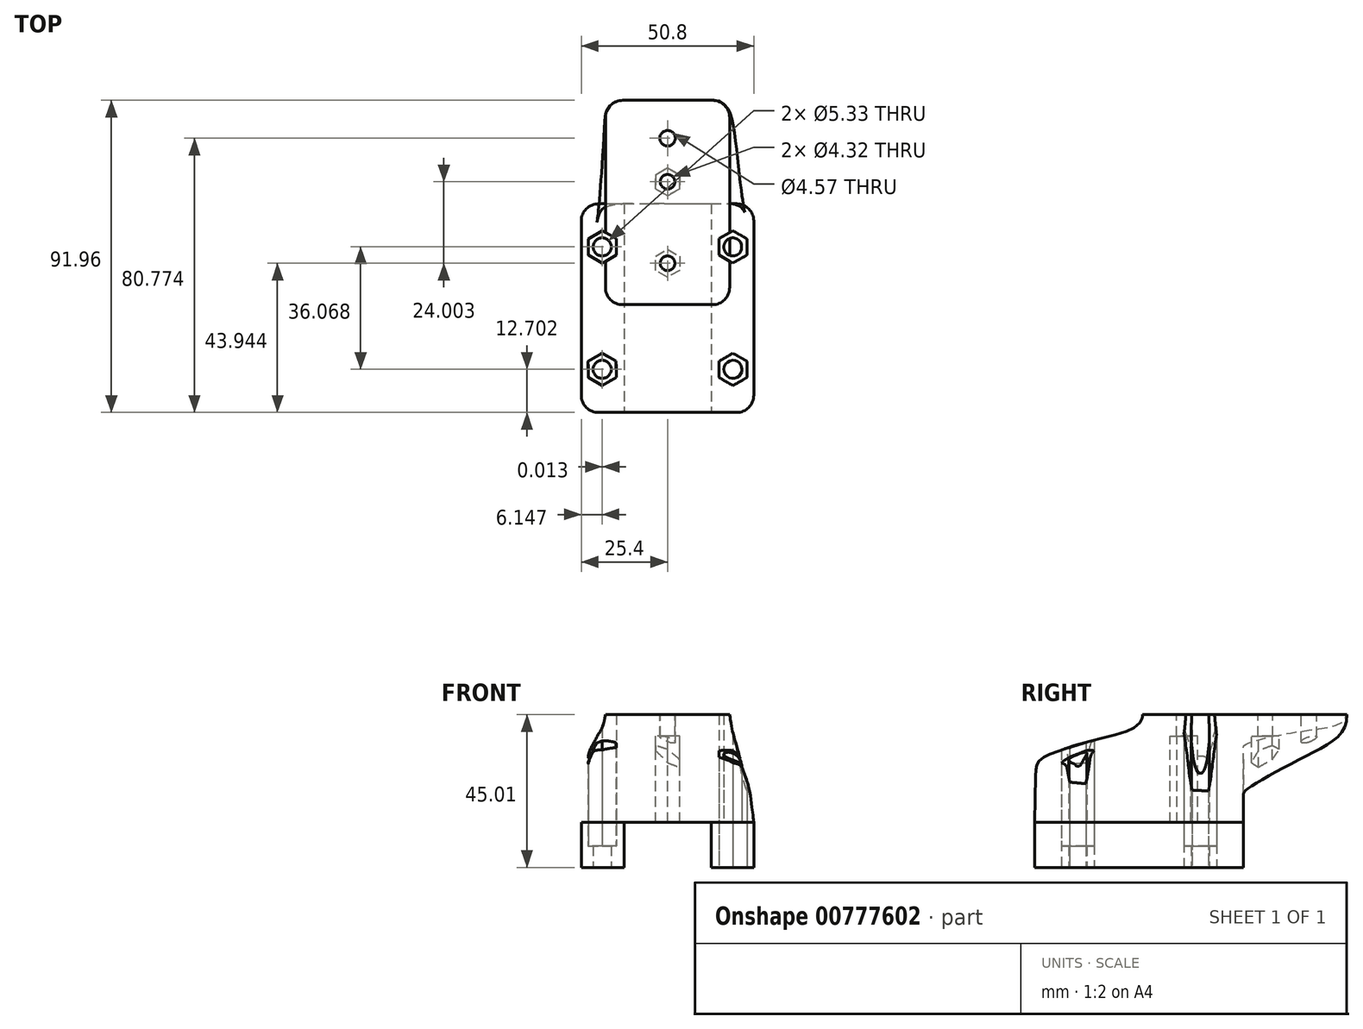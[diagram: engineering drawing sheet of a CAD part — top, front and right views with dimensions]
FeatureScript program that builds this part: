
annotation { "Feature Type Name" : "Feature", "Feature Type Description" : "" }
export const myFeature = defineFeature(function(context is Context, id is Id, definition is map)
    precondition{}
    {
        {
            var Q0;
            Q0=qCreatedBy(makeId("Top.planeOp"),FACE);
            var sketch = newSketch(context, id + "F0", { "sketchPlane" : qUnion([Q0])});
            skLineSegment(sketch, "E0.bottom", {"start": v(-20.32, 0) * mm, "end": v(20.32, 0) * mm});
            skLineSegment(sketch, "E0.top", {"start": v(-20.32, -61.47) * mm, "end": v(20.32, -61.47) * mm});
            skLineSegment(sketch, "E0.left", {"start": v(-25.4, -5.08) * mm, "end": v(-25.4, -56.39) * mm});
            skLineSegment(sketch, "E0.right", {"start": v(25.4, -5.08) * mm, "end": v(25.4, -56.39) * mm});
            skPoint(sketch, "E1.visualSharp", {"position": v(-25.4, 0) * mm});
            skArc(sketch, "E1.filletArc", {"start": v(-20.32, 0) * mm, "mid": v(-23.91, -1.49) * mm, "end": v(-25.4, -5.08) * mm});
            skPoint(sketch, "E2.visualSharp", {"position": v(25.4, 0) * mm});
            skArc(sketch, "E2.filletArc", {"start": v(25.4, -5.08) * mm, "mid": v(23.91, -1.49) * mm, "end": v(20.32, 0) * mm});
            skPoint(sketch, "E3.visualSharp", {"position": v(-25.4, -61.47) * mm});
            skArc(sketch, "E3.filletArc", {"start": v(-25.4, -56.39) * mm, "mid": v(-23.91, -59.98) * mm, "end": v(-20.32, -61.47) * mm});
            skPoint(sketch, "E4.visualSharp", {"position": v(25.4, -61.47) * mm});
            skArc(sketch, "E4.filletArc", {"start": v(20.32, -61.47) * mm, "mid": v(23.91, -59.98) * mm, "end": v(25.4, -56.39) * mm});
            skCircle(sketch, "E5", {"center": v(-19.24, -12.7) * mm, "radius": 2.67 * mm});
            skLineSegment(sketch, "E6.bottom", {"start": v(-12.83, 0) * mm, "end": v(12.83, 0) * mm});
            skLineSegment(sketch, "E6.top", {"start": v(-12.83, -61.47) * mm, "end": v(12.83, -61.47) * mm});
            skLineSegment(sketch, "E6.left", {"start": v(-12.83, 0) * mm, "end": v(-12.83, -61.47) * mm});
            skLineSegment(sketch, "E6.right", {"start": v(12.83, 0) * mm, "end": v(12.83, -61.47) * mm});
            skCircle(sketch, "E7.cCircle", {"center": v(-19.24, -12.7) * mm, "radius": 4.13 * mm, "construction": true});
            skLineSegment(sketch, "E7.0", {"start": v(-15.1, -15.06) * mm, "end": v(-19.22, -17.47) * mm});
            skLineSegment(sketch, "E7.1", {"start": v(-19.22, -17.47) * mm, "end": v(-23.36, -15.1) * mm});
            skLineSegment(sketch, "E7.2", {"start": v(-23.36, -15.1) * mm, "end": v(-23.38, -10.34) * mm});
            skLineSegment(sketch, "E7.3", {"start": v(-23.38, -10.34) * mm, "end": v(-19.26, -7.93) * mm});
            skLineSegment(sketch, "E7.4", {"start": v(-19.26, -7.93) * mm, "end": v(-15.12, -10.3) * mm});
            skLineSegment(sketch, "E7.5", {"start": v(-15.12, -10.3) * mm, "end": v(-15.1, -15.06) * mm});
            skPoint(sketch, "E7.0.midPoint", {"position": v(-17.16, -16.27) * mm});
            skCircle(sketch, "E8", {"center": v(-19.25, -48.77) * mm, "radius": 2.67 * mm});
            skCircle(sketch, "E9.cCircle", {"center": v(-19.25, -48.77) * mm, "radius": 4.13 * mm, "construction": true});
            skLineSegment(sketch, "E9.0", {"start": v(-15.12, -51.13) * mm, "end": v(-19.23, -53.53) * mm});
            skLineSegment(sketch, "E9.1", {"start": v(-19.23, -53.53) * mm, "end": v(-23.37, -51.17) * mm});
            skLineSegment(sketch, "E9.2", {"start": v(-23.37, -51.17) * mm, "end": v(-23.4, -46.4) * mm});
            skLineSegment(sketch, "E9.3", {"start": v(-23.4, -46.4) * mm, "end": v(-19.27, -44) * mm});
            skLineSegment(sketch, "E9.4", {"start": v(-19.27, -44) * mm, "end": v(-15.14, -46.37) * mm});
            skLineSegment(sketch, "E9.5", {"start": v(-15.14, -46.37) * mm, "end": v(-15.12, -51.13) * mm});
            skPoint(sketch, "E9.0.midPoint", {"position": v(-17.17, -52.33) * mm});
            skLineSegment(sketch, "E10.MirrorCS", {"start": v(23.36, -15.1) * mm, "end": v(23.38, -10.34) * mm});
            skLineSegment(sketch, "E11.MirrorCS", {"start": v(23.4, -46.4) * mm, "end": v(19.27, -44) * mm});
            skLineSegment(sketch, "E12.MirrorCS", {"start": v(23.37, -51.17) * mm, "end": v(23.4, -46.4) * mm});
            skLineSegment(sketch, "E13.MirrorCS", {"start": v(19.27, -44) * mm, "end": v(15.14, -46.37) * mm});
            skLineSegment(sketch, "E14.MirrorCS", {"start": v(23.38, -10.34) * mm, "end": v(19.26, -7.93) * mm});
            skLineSegment(sketch, "E15.MirrorCS", {"start": v(15.1, -15.06) * mm, "end": v(19.22, -17.47) * mm});
            skLineSegment(sketch, "E16.MirrorCS", {"start": v(19.26, -7.93) * mm, "end": v(15.12, -10.3) * mm});
            skLineSegment(sketch, "E17.MirrorCS", {"start": v(19.22, -17.47) * mm, "end": v(23.36, -15.1) * mm});
            skLineSegment(sketch, "E18.MirrorCS", {"start": v(15.14, -46.37) * mm, "end": v(15.12, -51.13) * mm});
            skLineSegment(sketch, "E19.MirrorCS", {"start": v(15.12, -51.13) * mm, "end": v(19.23, -53.53) * mm});
            skLineSegment(sketch, "E20.MirrorCS", {"start": v(19.23, -53.53) * mm, "end": v(23.37, -51.17) * mm});
            skLineSegment(sketch, "E21.MirrorCS", {"start": v(15.12, -10.3) * mm, "end": v(15.1, -15.06) * mm});
            skCircle(sketch, "E22.MirrorC", {"center": v(19.25, -48.77) * mm, "radius": 2.67 * mm});
            skCircle(sketch, "E23.MirrorC", {"center": v(19.24, -12.7) * mm, "radius": 4.13 * mm, "construction": true});
            skPoint(sketch, "E24.MirrorP", {"position": v(17.16, -16.27) * mm});
            skCircle(sketch, "E25.MirrorC", {"center": v(19.24, -12.7) * mm, "radius": 2.67 * mm});
            skCircle(sketch, "E26.MirrorC", {"center": v(19.25, -48.77) * mm, "radius": 4.13 * mm, "construction": true});
            skPoint(sketch, "E27.MirrorP", {"position": v(17.17, -52.33) * mm});
            skSolve(sketch);
        }
        {
            var Q0;
            Q0=qCreatedBy(makeId("Top.planeOp"),FACE);
            cPlane(context, id + "F1", {"entities" : qUnion([Q0]), "cplaneType" : CPlaneType.OFFSET, "offset" : 31.75 * mm, "width" : 152.4 * mm, "height" : 152.4 * mm});
        }
        {
            var Q0;
            Q0=qCreatedBy(id+"F1.planeOp",FACE);
            var sketch = newSketch(context, id + "F2", { "sketchPlane" : qUnion([Q0])});
            skCircle(sketch, "E28", {"center": v(0, 19.3) * mm, "radius": 2.29 * mm});
            skCircle(sketch, "E29", {"center": v(0, 6.48) * mm, "radius": 2.16 * mm});
            skCircle(sketch, "E30", {"center": v(0, -17.53) * mm, "radius": 2.16 * mm});
            skLineSegment(sketch, "E31.bottom", {"start": v(-13.2, 30.48) * mm, "end": v(13.2, 30.48) * mm});
            skLineSegment(sketch, "E31.top", {"start": v(-13.2, -29.72) * mm, "end": v(13.2, -29.72) * mm});
            skLineSegment(sketch, "E31.left", {"start": v(-18.29, 25.4) * mm, "end": v(-18.29, -24.64) * mm});
            skLineSegment(sketch, "E31.right", {"start": v(18.29, 25.4) * mm, "end": v(18.29, -24.64) * mm});
            skCircle(sketch, "E32.cCircle", {"center": v(0, 6.48) * mm, "radius": 3.55 * mm, "construction": true});
            skLineSegment(sketch, "E32.0", {"start": v(3.55, 8.53) * mm, "end": v(3.55, 4.43) * mm});
            skLineSegment(sketch, "E32.1", {"start": v(3.55, 4.43) * mm, "end": v(0, 2.38) * mm});
            skLineSegment(sketch, "E32.2", {"start": v(0, 2.38) * mm, "end": v(-3.55, 4.43) * mm});
            skLineSegment(sketch, "E32.3", {"start": v(-3.55, 4.43) * mm, "end": v(-3.55, 8.53) * mm});
            skLineSegment(sketch, "E32.4", {"start": v(-3.55, 8.53) * mm, "end": v(0, 10.58) * mm});
            skLineSegment(sketch, "E32.5", {"start": v(0, 10.58) * mm, "end": v(3.55, 8.53) * mm});
            skCircle(sketch, "E33.cCircle", {"center": v(0, -17.53) * mm, "radius": 3.55 * mm, "construction": true});
            skLineSegment(sketch, "E33.0", {"start": v(-3.55, -19.58) * mm, "end": v(-3.55, -15.48) * mm});
            skLineSegment(sketch, "E33.1", {"start": v(-3.55, -15.48) * mm, "end": v(0, -13.43) * mm});
            skLineSegment(sketch, "E33.2", {"start": v(0, -13.43) * mm, "end": v(3.55, -15.48) * mm});
            skLineSegment(sketch, "E33.3", {"start": v(3.55, -15.48) * mm, "end": v(3.55, -19.58) * mm});
            skLineSegment(sketch, "E33.4", {"start": v(3.55, -19.58) * mm, "end": v(0, -21.63) * mm});
            skLineSegment(sketch, "E33.5", {"start": v(0, -21.63) * mm, "end": v(-3.55, -19.58) * mm});
            skArc(sketch, "E34.filletArc", {"start": v(-13.2, 30.48) * mm, "mid": v(-16.8, 29) * mm, "end": v(-18.29, 25.4) * mm});
            skArc(sketch, "E35.filletArc", {"start": v(18.29, 25.4) * mm, "mid": v(16.8, 29) * mm, "end": v(13.2, 30.48) * mm});
            skArc(sketch, "E36.filletArc", {"start": v(13.2, -29.72) * mm, "mid": v(16.8, -28.23) * mm, "end": v(18.29, -24.64) * mm});
            skArc(sketch, "E37.filletArc", {"start": v(-18.29, -24.64) * mm, "mid": v(-16.8, -28.23) * mm, "end": v(-13.2, -29.72) * mm});
            skPoint(sketch, "E38.startSnap0", {"position": v(-18.29, 0.38) * mm});
            skSolve(sketch);
        }
        {
            var Q0;
            Q0=qCreatedBy(makeId("Top.planeOp"),FACE);
            var sketch = newSketch(context, id + "F3", { "sketchPlane" : qUnion([Q0])});
            skLineSegment(sketch, "E39.bottom", {"start": v(-20.32, 0) * mm, "end": v(20.32, 0) * mm});
            skLineSegment(sketch, "E39.top", {"start": v(-20.32, -61.47) * mm, "end": v(20.32, -61.47) * mm});
            skLineSegment(sketch, "E39.left", {"start": v(-25.4, -5.08) * mm, "end": v(-25.4, -56.39) * mm});
            skLineSegment(sketch, "E39.right", {"start": v(25.4, -5.08) * mm, "end": v(25.4, -56.39) * mm});
            skPoint(sketch, "E40.visualSharp", {"position": v(-25.4, 0) * mm});
            skArc(sketch, "E40.filletArc", {"start": v(-20.32, 0) * mm, "mid": v(-23.91, -1.49) * mm, "end": v(-25.4, -5.08) * mm});
            skPoint(sketch, "E41.visualSharp", {"position": v(25.4, 0) * mm});
            skArc(sketch, "E41.filletArc", {"start": v(25.4, -5.08) * mm, "mid": v(23.91, -1.49) * mm, "end": v(20.32, 0) * mm});
            skPoint(sketch, "E42.visualSharp", {"position": v(25.4, -61.47) * mm});
            skArc(sketch, "E42.filletArc", {"start": v(20.32, -61.47) * mm, "mid": v(23.91, -59.98) * mm, "end": v(25.4, -56.39) * mm});
            skPoint(sketch, "E43.visualSharp", {"position": v(-25.4, -61.47) * mm});
            skArc(sketch, "E43.filletArc", {"start": v(-25.4, -56.39) * mm, "mid": v(-23.91, -59.98) * mm, "end": v(-20.32, -61.47) * mm});
            skSolve(sketch);
        }
        {
            var Q0;
            Q0=qCreatedBy(id+"F1.planeOp",FACE);
            var sketch = newSketch(context, id + "F4", { "sketchPlane" : qUnion([Q0])});
            skLineSegment(sketch, "E44.bottom", {"start": v(13.2, 30.48) * mm, "end": v(-13.2, 30.48) * mm});
            skLineSegment(sketch, "E44.top", {"start": v(13.2, -29.72) * mm, "end": v(-13.2, -29.72) * mm});
            skLineSegment(sketch, "E44.left", {"start": v(18.29, 25.4) * mm, "end": v(18.29, -24.64) * mm});
            skLineSegment(sketch, "E44.right", {"start": v(-18.29, 25.4) * mm, "end": v(-18.29, -24.64) * mm});
            skPoint(sketch, "E45.visualSharp", {"position": v(18.29, 30.48) * mm});
            skArc(sketch, "E45.filletArc", {"start": v(18.29, 25.4) * mm, "mid": v(16.8, 29) * mm, "end": v(13.2, 30.48) * mm});
            skPoint(sketch, "E46.visualSharp", {"position": v(-18.29, 30.48) * mm});
            skArc(sketch, "E46.filletArc", {"start": v(-13.2, 30.48) * mm, "mid": v(-16.8, 29) * mm, "end": v(-18.29, 25.4) * mm});
            skPoint(sketch, "E47.visualSharp", {"position": v(-18.29, -29.72) * mm});
            skArc(sketch, "E47.filletArc", {"start": v(-18.29, -24.64) * mm, "mid": v(-16.8, -28.23) * mm, "end": v(-13.2, -29.72) * mm});
            skPoint(sketch, "E48.visualSharp", {"position": v(18.29, -29.72) * mm});
            skArc(sketch, "E48.filletArc", {"start": v(13.2, -29.72) * mm, "mid": v(16.8, -28.23) * mm, "end": v(18.29, -24.64) * mm});
            skSolve(sketch);
        }
        {
            var Q0;
            Q0=qCreatedBy(makeId("Front.planeOp"),FACE);
            var sketch = newSketch(context, id + "F5", { "sketchPlane" : qUnion([Q0])});
            skFitSpline(sketch, "E49", {"points": [v(20.45, 0) * mm, v(12.83, 9.22) * mm, v(11.26, 9.9) * mm, v(-22.15, 25.9) * mm], "startDerivative": vector(0.57, 58.48) * mm, "endDerivative": vector(-118.47, 55.1) * mm});
            skLineSegment(sketch, "E50", {"start": v(0, 0) * mm, "end": v(0, 15.6) * mm});
            skLineSegment(sketch, "E51", {"start": v(-22.15, 25.9) * mm, "end": v(-22.15, 0) * mm});
            skLineSegment(sketch, "E52", {"start": v(12.83, 0) * mm, "end": v(12.83, 9.22) * mm});
            skSolve(sketch);
        }
        {
            var Q0;
            Q0=sQuery(id+"F5.wireOp",VERTEX,"E52.end");
            var Q1;
            Q1=sQuery(id+"F0.wireOp",VERTEX,"E6.bottom.end");
            var Q2;
            Q2=sQuery(id+"F0.wireOp",VERTEX,"E6.top.end");
            cPlane(context, id + "F6", {"entities" : qUnion([Q0, Q1, Q2]), "cplaneType" : CPlaneType.THREE_POINT, "offset" : 25.4 * mm, "width" : 152.4 * mm, "height" : 152.4 * mm});
        }
        {
            var Q0;
            Q0=qCreatedBy(id+"F6.planeOp",FACE);
            var sketch = newSketch(context, id + "F7", { "sketchPlane" : qUnion([Q0])});
            skFitSpline(sketch, "E53", {"points": [v(0, 0) * mm, v(0, 8.03) * mm, v(0.77, 9.54) * mm, v(18.88, 19.75) * mm, v(30.48, 31.75) * mm], "startDerivative": vector(0, 51.84) * mm, "endDerivative": vector(-2.78, 57.28) * mm});
            skLineSegment(sketch, "E54", {"start": v(30.48, 31.75) * mm, "end": v(-29.72, 31.75) * mm});
            skLineSegment(sketch, "E55", {"start": v(-29.72, 31.75) * mm, "end": v(-61.47, 0) * mm});
            skLineSegment(sketch, "E56", {"start": v(-61.47, 0) * mm, "end": v(0, 0) * mm});
            skSolve(sketch);
        }
        {
            var Q0;
            Q0=qCreatedBy(makeId("Right.planeOp"),FACE);
            var Q1;
            Q1=sQuery(id+"F4.wireOp",VERTEX,"E44.bottom.end");
            cPlane(context, id + "F8", {"entities" : qUnion([Q0, Q1]), "cplaneType" : CPlaneType.PLANE_POINT, "offset" : 25.4 * mm, "width" : 152.4 * mm, "height" : 152.4 * mm});
        }
        {
            var Q0;
            Q0=qCreatedBy(id+"F8.planeOp",FACE);
            var sketch = newSketch(context, id + "F9", { "sketchPlane" : qUnion([Q0])});
            skFitSpline(sketch, "E57", {"points": [v(0, 0) * mm, v(0, 21.64) * mm, v(0.4, 22.85) * mm, v(18.32, 27.03) * mm, v(30.48, 31.75) * mm], "startDerivative": vector(0, 100.73) * mm, "endDerivative": vector(0.43, 39.9) * mm});
            skLineSegment(sketch, "E58", {"start": v(30.48, 31.75) * mm, "end": v(-29.73, 31.75) * mm});
            skLineSegment(sketch, "E59", {"start": v(-29.72, 31.75) * mm, "end": v(-61.47, 0) * mm});
            skLineSegment(sketch, "E60", {"start": v(-61.47, 0) * mm, "end": v(0, 0) * mm});
            skSolve(sketch);
        }
        {
            var Q0;
            Q0=makeQuery(id+"F3.imprint","IMPRINT",FACE,{"disambiguationData":[TD([[makeQuery(id+"F3.imprint","IMPRINT",EDGE,{"derivedFrom":sQuery(id+"F3.wireOp",EDGE,"E39.bottom")}),-1.0]])]});
            var Q1;
            Q1=makeQuery(id+"F4.imprint","IMPRINT",FACE,{"disambiguationData":[TD([[makeQuery(id+"F4.imprint","IMPRINT",EDGE,{"derivedFrom":sQuery(id+"F4.wireOp",EDGE,"E44.bottom")}),1.0]])]});
            var Q2;
            Q2=sQuery(id+"F7.wireOp",EDGE,"E53");
            var Q3;
            Q3=sQuery(id+"F9.wireOp",EDGE,"E57");
            loft(context, id + "F10", {"addGuides" : true, "sheetProfilesArray" : [{ "sheetProfileEntities" : qUnion([Q0]) }, { "sheetProfileEntities" : qUnion([Q1]) }], "guidesArray" : [{ "guideEntities" : qUnion([Q2]), "guideDerivativeType" : LoftGuideDerivativeType.DEFAULT, "guideDerivativeMagnitude" : 1 }, { "guideEntities" : qUnion([Q3]), "guideDerivativeType" : LoftGuideDerivativeType.DEFAULT, "guideDerivativeMagnitude" : 1 }]});
        }
        {
            var Q0;
            Q0=makeQuery(id+"F2.imprint","IMPRINT",FACE,{"disambiguationData":[TD([[makeQuery(id+"F2.imprint","IMPRINT",EDGE,{"derivedFrom":sQuery(id+"F2.wireOp",EDGE,"E28")}),1.0]])]});
            var Q1;
            Q1=makeQuery(id+"F2.imprint","IMPRINT",FACE,{"disambiguationData":[TD([[makeQuery(id+"F2.imprint","IMPRINT",EDGE,{"derivedFrom":sQuery(id+"F2.wireOp",EDGE,"E29")}),1.0]])]});
            var Q2;
            Q2=makeQuery(id+"F2.imprint","IMPRINT",FACE,{"disambiguationData":[TD([[makeQuery(id+"F2.imprint","IMPRINT",EDGE,{"derivedFrom":sQuery(id+"F2.wireOp",EDGE,"E30")}),1.0]])]});
            extrude(context, id + "F11", {"entities" : qUnion([Q0, Q1, Q2]), "operationType" : NewBodyOperationType.REMOVE, "endBound" : BoundingType.THROUGH_ALL, "oppositeDirection" : true, "depth" : 25.4 * mm, "offsetDistance" : 25.4 * mm});
        }
        {
            var Q0;
            Q0=makeQuery(id+"F0.imprint","IMPRINT",FACE,{"disambiguationData":[TD([[makeQuery(id+"F0.imprint","IMPRINT",EDGE,{"derivedFrom":sQuery(id+"F0.wireOp",EDGE,"E0.left")}),1.0]])]});
            var Q1;
            Q1=makeQuery(id+"F0.imprint","IMPRINT",FACE,{"disambiguationData":[TD([[makeQuery(id+"F0.imprint","IMPRINT",EDGE,{"derivedFrom":sQuery(id+"F0.wireOp",EDGE,"E5")}),-1.0]])]});
            var Q2;
            Q2=makeQuery(id+"F0.imprint","IMPRINT",FACE,{"disambiguationData":[TD([[makeQuery(id+"F0.imprint","IMPRINT",EDGE,{"derivedFrom":sQuery(id+"F0.wireOp",EDGE,"E5")}),1.0]])]});
            var Q3;
            Q3=makeQuery(id+"F0.imprint","IMPRINT",FACE,{"disambiguationData":[TD([[makeQuery(id+"F0.imprint","IMPRINT",EDGE,{"derivedFrom":sQuery(id+"F0.wireOp",EDGE,"E8")}),1.0]])]});
            var Q4;
            Q4=makeQuery(id+"F0.imprint","IMPRINT",FACE,{"disambiguationData":[TD([[makeQuery(id+"F0.imprint","IMPRINT",EDGE,{"derivedFrom":sQuery(id+"F0.wireOp",EDGE,"E8")}),-1.0]])]});
            var Q5;
            Q5=makeQuery(id+"F0.imprint","IMPRINT",FACE,{"disambiguationData":[TD([[makeQuery(id+"F0.imprint","IMPRINT",EDGE,{"derivedFrom":sQuery(id+"F0.wireOp",EDGE,"E22.MirrorC")}),-1.0]])]});
            var Q6;
            Q6=makeQuery(id+"F0.imprint","IMPRINT",FACE,{"disambiguationData":[TD([[makeQuery(id+"F0.imprint","IMPRINT",EDGE,{"derivedFrom":sQuery(id+"F0.wireOp",EDGE,"E11.MirrorCS")}),1.0]])]});
            var Q7;
            Q7=makeQuery(id+"F0.imprint","IMPRINT",FACE,{"disambiguationData":[TD([[makeQuery(id+"F0.imprint","IMPRINT",EDGE,{"derivedFrom":sQuery(id+"F0.wireOp",EDGE,"E0.right")}),-1.0]])]});
            var Q8;
            Q8=makeQuery(id+"F0.imprint","IMPRINT",FACE,{"disambiguationData":[TD([[makeQuery(id+"F0.imprint","IMPRINT",EDGE,{"derivedFrom":sQuery(id+"F0.wireOp",EDGE,"E25.MirrorC")}),-1.0]])]});
            var Q9;
            Q9=makeQuery(id+"F0.imprint","IMPRINT",FACE,{"disambiguationData":[TD([[makeQuery(id+"F0.imprint","IMPRINT",EDGE,{"derivedFrom":sQuery(id+"F0.wireOp",EDGE,"E10.MirrorCS")}),1.0]])]});
            extrude(context, id + "F12", {"entities" : qUnion([Q0, Q1, Q2, Q3, Q4, Q5, Q6, Q7, Q8, Q9]), "operationType" : NewBodyOperationType.ADD, "oppositeDirection" : true, "depth" : 13.26 * mm, "offsetDistance" : 25.4 * mm});
        }
        {
            var Q0;
            Q0=makeQuery(id+"F0.imprint","IMPRINT",FACE,{"disambiguationData":[TD([[makeQuery(id+"F0.imprint","IMPRINT",EDGE,{"derivedFrom":sQuery(id+"F0.wireOp",EDGE,"E25.MirrorC")}),-1.0]])]});
            var Q1;
            Q1=makeQuery(id+"F0.imprint","IMPRINT",FACE,{"disambiguationData":[TD([[makeQuery(id+"F0.imprint","IMPRINT",EDGE,{"derivedFrom":sQuery(id+"F0.wireOp",EDGE,"E22.MirrorC")}),-1.0]])]});
            var Q2;
            Q2=makeQuery(id+"F0.imprint","IMPRINT",FACE,{"disambiguationData":[TD([[makeQuery(id+"F0.imprint","IMPRINT",EDGE,{"derivedFrom":sQuery(id+"F0.wireOp",EDGE,"E5")}),1.0]])]});
            var Q3;
            Q3=makeQuery(id+"F0.imprint","IMPRINT",FACE,{"disambiguationData":[TD([[makeQuery(id+"F0.imprint","IMPRINT",EDGE,{"derivedFrom":sQuery(id+"F0.wireOp",EDGE,"E8")}),1.0]])]});
            extrude(context, id + "F13", {"entities" : qUnion([Q0, Q1, Q2, Q3]), "operationType" : NewBodyOperationType.REMOVE, "endBound" : BoundingType.THROUGH_ALL, "depth" : 25.4 * mm, "offsetDistance" : 25.4 * mm, "hasSecondDirection" : true, "secondDirectionBound" : SecondDirectionBoundingType.THROUGH_ALL, "secondDirectionOppositeDirection" : true, "secondDirectionDepth" : 25.4 * mm});
        }
        {
            var Q0;
            Q0=makeQuery(id+"F0.imprint","IMPRINT",FACE,{"disambiguationData":[TD([[makeQuery(id+"F0.imprint","IMPRINT",EDGE,{"derivedFrom":sQuery(id+"F0.wireOp",EDGE,"E10.MirrorCS")}),1.0]])]});
            var Q1;
            Q1=makeQuery(id+"F0.imprint","IMPRINT",FACE,{"disambiguationData":[TD([[makeQuery(id+"F0.imprint","IMPRINT",EDGE,{"derivedFrom":sQuery(id+"F0.wireOp",EDGE,"E5")}),-1.0]])]});
            var Q2;
            Q2=makeQuery(id+"F0.imprint","IMPRINT",FACE,{"disambiguationData":[TD([[makeQuery(id+"F0.imprint","IMPRINT",EDGE,{"derivedFrom":sQuery(id+"F0.wireOp",EDGE,"E11.MirrorCS")}),1.0]])]});
            var Q3;
            Q3=makeQuery(id+"F0.imprint","IMPRINT",FACE,{"disambiguationData":[TD([[makeQuery(id+"F0.imprint","IMPRINT",EDGE,{"derivedFrom":sQuery(id+"F0.wireOp",EDGE,"E8")}),-1.0]])]});
            extrude(context, id + "F14", {"entities" : qUnion([Q0, Q1, Q2, Q3]), "operationType" : NewBodyOperationType.REMOVE, "endBound" : BoundingType.THROUGH_ALL, "depth" : 25.4 * mm, "offsetDistance" : 25.4 * mm, "hasSecondDirection" : true, "secondDirectionOppositeDirection" : true, "secondDirectionDepth" : 6.9 * mm});
        }
        {
            var Q0;
            Q0=makeQuery(id+"F2.imprint","IMPRINT",FACE,{"disambiguationData":[TD([[makeQuery(id+"F2.imprint","IMPRINT",EDGE,{"derivedFrom":sQuery(id+"F2.wireOp",EDGE,"E30")}),-1.0]])]});
            var Q1;
            Q1=makeQuery(id+"F2.imprint","IMPRINT",FACE,{"disambiguationData":[TD([[makeQuery(id+"F2.imprint","IMPRINT",EDGE,{"derivedFrom":sQuery(id+"F2.wireOp",EDGE,"E29")}),-1.0]])]});
            extrude(context, id + "F15", {"entities" : qUnion([Q0, Q1]), "operationType" : NewBodyOperationType.REMOVE, "endBound" : BoundingType.THROUGH_ALL, "oppositeDirection" : true, "depth" : 25.4 * mm, "offsetDistance" : 25.4 * mm, "hasSecondDirection" : true, "secondDirectionOppositeDirection" : true, "secondDirectionDepth" : 6.35 * mm});
        }
    });
